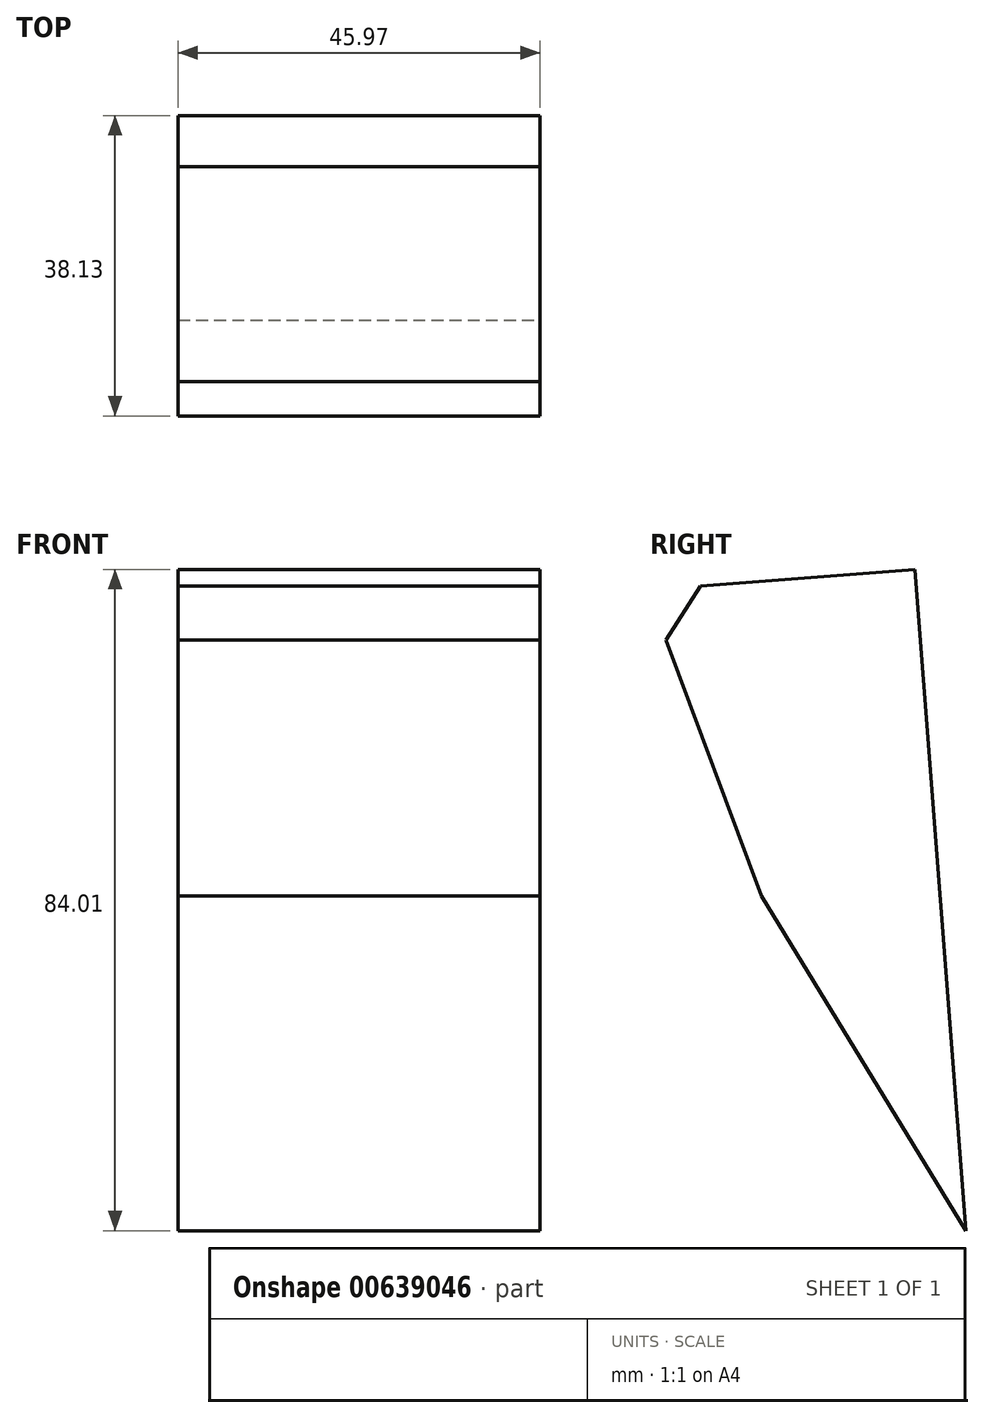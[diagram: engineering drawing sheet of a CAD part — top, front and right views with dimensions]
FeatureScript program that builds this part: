
annotation { "Feature Type Name" : "Feature", "Feature Type Description" : "" }
export const myFeature = defineFeature(function(context is Context, id is Id, definition is map)
    precondition{}
    {
        {
            var Q0;
            Q0=qCreatedBy(makeId("Right.planeOp"),FACE);
            var sketch = newSketch(context, id + "F0", { "sketchPlane" : qUnion([Q0])});
            skLineSegment(sketch, "E0", {"start": v(-15.56, -7.27) * mm, "end": v(-30.09, 31.58) * mm});
            skLineSegment(sketch, "E1", {"start": v(-30.09, 31.58) * mm, "end": v(3.91, 34.2) * mm});
            skLineSegment(sketch, "E2", {"start": v(3.91, 34.2) * mm, "end": v(10.41, -49.8) * mm});
            skLineSegment(sketch, "E3", {"start": v(10.41, -49.8) * mm, "end": v(-15.56, -7.27) * mm});
            skSolve(sketch);
        }
        {
            var Q0;
            Q0=makeQuery(id+"F0.imprint","IMPRINT",FACE,{"disambiguationData":[TD([[makeQuery(id+"F0.imprint","IMPRINT",EDGE,{"derivedFrom":sQuery(id+"F0.wireOp",EDGE,"E0")}),-1.0]])]});
            extrude(context, id + "F1", {"entities" : qUnion([Q0]), "oppositeDirection" : true, "depth" : 45.97 * mm, "offsetDistance" : 25.4 * mm});
        }
        {
            var Q0;
            Q0=makeQuery(id+"F1.opExtrude","SWEPT_EDGE",EDGE,{"disambiguationData":[OSD([sQuery(id+"F0.wireOp",EDGE,"E0"),sQuery(id+"F0.wireOp",EDGE,"E1")])]});
            chamfer(context, id + "F2", {"entities" : qUnion([Q0]), "width" : 5.08 * mm, "tangentPropagation" : true});
        }
    });
